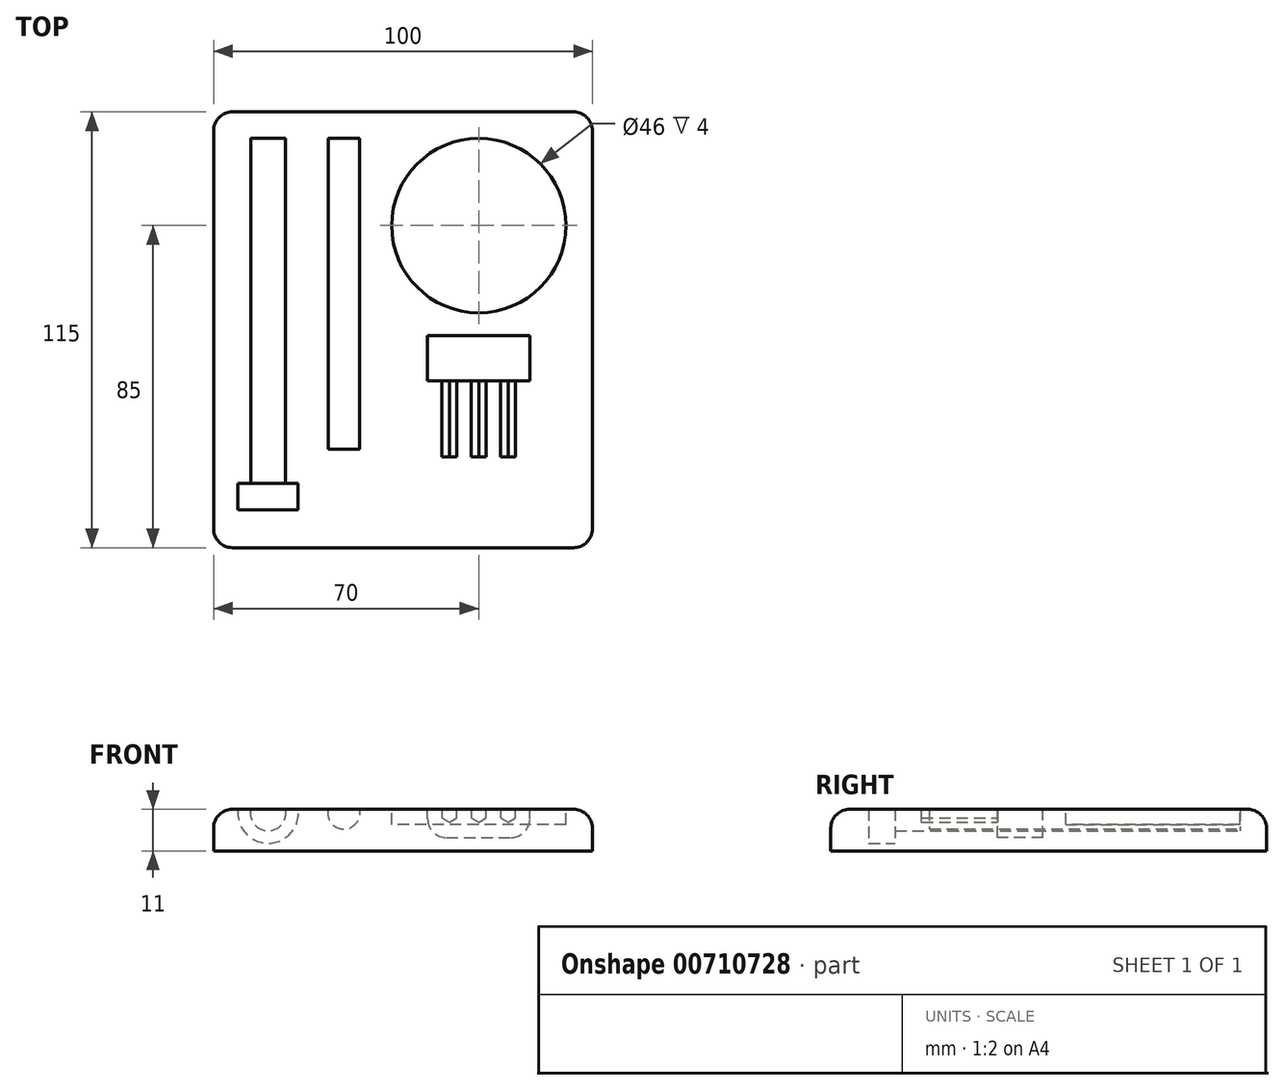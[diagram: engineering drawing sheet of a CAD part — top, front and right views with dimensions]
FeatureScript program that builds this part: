
annotation { "Feature Type Name" : "Feature", "Feature Type Description" : "" }
export const myFeature = defineFeature(function(context is Context, id is Id, definition is map)
    precondition{}
    {
        {
            var Q0;
            Q0=qCreatedBy(makeId("Top.planeOp"),FACE);
            var sketch = newSketch(context, id + "F0", { "sketchPlane" : qUnion([Q0])});
            skLineSegment(sketch, "E0.bottom", {"start": v(0, 0) * mm, "end": v(100, 0) * mm});
            skLineSegment(sketch, "E0.top", {"start": v(0, 115) * mm, "end": v(100, 115) * mm});
            skLineSegment(sketch, "E0.left", {"start": v(0, 0) * mm, "end": v(0, 115) * mm});
            skLineSegment(sketch, "E0.right", {"start": v(100, 0) * mm, "end": v(100, 115) * mm});
            skSolve(sketch);
        }
        {
            var Q0;
            Q0=makeQuery(id+"F0.imprint","IMPRINT",FACE,{"disambiguationData":[TD([[makeQuery(id+"F0.imprint","IMPRINT",EDGE,{"derivedFrom":sQuery(id+"F0.wireOp",EDGE,"E0.bottom")}),1.0]])]});
            extrude(context, id + "F1", {"entities" : qUnion([Q0]), "depth" : 15 * mm, "offsetDistance" : 25 * mm});
        }
        {
            var Q0;
            Q0=makeQuery(id+"F1.opExtrude","CAP_FACE",FACE,{"disambiguationData":[OSD([sQuery(id+"F0.wireOp",EDGE,"E0.bottom"),sQuery(id+"F0.wireOp",EDGE,"E0.top"),sQuery(id+"F0.wireOp",EDGE,"E0.left"),sQuery(id+"F0.wireOp",EDGE,"E0.right")])],"isStart":false});
            var sketch = newSketch(context, id + "F2", { "sketchPlane" : qUnion([Q0])});
            skCircle(sketch, "E1", {"center": v(70, 85) * mm, "radius": 23 * mm});
            skSolve(sketch);
        }
        {
            var Q0;
            Q0=makeQuery(id+"F2.imprint","IMPRINT",FACE,{"disambiguationData":[TD([[makeQuery(id+"F2.imprint","IMPRINT",EDGE,{"derivedFrom":sQuery(id+"F2.wireOp",EDGE,"E1")}),1.0]])]});
            extrude(context, id + "F3", {"entities" : qUnion([Q0]), "operationType" : NewBodyOperationType.REMOVE, "oppositeDirection" : true, "depth" : 4 * mm, "offsetDistance" : 25 * mm});
        }
        {
            var Q0;
            Q0=makeQuery(id+"F1.opExtrude","SWEPT_FACE",FACE,{"disambiguationData":[OSD([sQuery(id+"F0.wireOp",EDGE,"E0.top")])]});
            cPlane(context, id + "F4", {"entities" : qUnion([Q0]), "cplaneType" : CPlaneType.OFFSET, "offset" : 7 * mm, "oppositeDirection" : true, "width" : 150 * mm, "height" : 150 * mm});
        }
        {
            var Q0;
            Q0=qCreatedBy(id+"F4.planeOp",FACE);
            var sketch = newSketch(context, id + "F5", { "sketchPlane" : qUnion([Q0])});
            skCircle(sketch, "E2", {"center": v(-14.4, 14) * mm, "radius": 4.7 * mm});
            skSolve(sketch);
        }
        {
            var Q0;
            Q0=makeQuery(id+"F5.imprint","IMPRINT",FACE,{"disambiguationData":[TD([[makeQuery(id+"F5.imprint","IMPRINT",EDGE,{"derivedFrom":sQuery(id+"F5.wireOp",EDGE,"E2")}),1.0]])]});
            extrude(context, id + "F6", {"entities" : qUnion([Q0]), "operationType" : NewBodyOperationType.REMOVE, "oppositeDirection" : true, "depth" : 91 * mm, "offsetDistance" : 25 * mm});
        }
        {
            var Q0;
            Q0=makeQuery(id+"F6.boolean.opBoolean","COPY",FACE,{"derivedFrom":makeQuery(id+"F6.opExtrude","CAP_FACE",FACE,{"disambiguationData":[OSD([sQuery(id+"F5.wireOp",EDGE,"E2")])],"isStart":false})});
            var sketch = newSketch(context, id + "F7", { "sketchPlane" : qUnion([Q0])});
            skCircle(sketch, "E3", {"center": v(-14.4, 14) * mm, "radius": 8 * mm});
            skSolve(sketch);
        }
        {
            var Q0;
            {var subQ0=sQuery(id+"F5.wireOp",EDGE,"E2");Q0=makeQuery(id+"F7.imprint","IMPRINT",FACE,{"disambiguationData":[TD([[makeQuery(id+"F7.imprint","IMPRINT",EDGE,{"derivedFrom":makeQuery(id+"F6.boolean.opBoolean","COPY",EDGE,{"derivedFrom":makeQuery(id+"F6.opExtrude","CAP_EDGE",EDGE,{"disambiguationData":[OSD([subQ0])],"isStart":false})})}),1.0]])]});}
            var Q1;
            Q1=makeQuery(id+"F7.imprint","IMPRINT",FACE,{"disambiguationData":[TD([[makeQuery(id+"F7.imprint","IMPRINT",EDGE,{"derivedFrom":sQuery(id+"F7.wireOp",EDGE,"E3")}),1.0]])]});
            extrude(context, id + "F8", {"entities" : qUnion([Q0, Q1]), "operationType" : NewBodyOperationType.REMOVE, "oppositeDirection" : true, "depth" : 7 * mm, "offsetDistance" : 25 * mm});
        }
        {
            var Q0;
            Q0=qCreatedBy(id+"F4.planeOp",FACE);
            var sketch = newSketch(context, id + "F9", { "sketchPlane" : qUnion([Q0])});
            skCircle(sketch, "E4", {"center": v(-34.4, 14) * mm, "radius": 4.25 * mm});
            skSolve(sketch);
        }
        {
            var Q0;
            Q0=makeQuery(id+"F9.imprint","IMPRINT",FACE,{"disambiguationData":[TD([[makeQuery(id+"F9.imprint","IMPRINT",EDGE,{"derivedFrom":sQuery(id+"F9.wireOp",EDGE,"E4")}),1.0]])]});
            extrude(context, id + "F10", {"entities" : qUnion([Q0]), "operationType" : NewBodyOperationType.REMOVE, "oppositeDirection" : true, "depth" : 82 * mm, "offsetDistance" : 25 * mm});
        }
        {
            var Q0;
            Q0=makeQuery(id+"F1.opExtrude","CAP_FACE",FACE,{"disambiguationData":[OSD([sQuery(id+"F0.wireOp",EDGE,"E0.bottom"),sQuery(id+"F0.wireOp",EDGE,"E0.top"),sQuery(id+"F0.wireOp",EDGE,"E0.left"),sQuery(id+"F0.wireOp",EDGE,"E0.right")])],"isStart":false});
            var sketch = newSketch(context, id + "F11", { "sketchPlane" : qUnion([Q0])});
            skLineSegment(sketch, "E5.bottom", {"start": v(56.5, 52) * mm, "end": v(83.5, 52) * mm});
            skLineSegment(sketch, "E5.top", {"start": v(56.5, 44) * mm, "end": v(83.5, 44) * mm});
            skLineSegment(sketch, "E5.left", {"start": v(56.5, 52) * mm, "end": v(56.5, 44) * mm});
            skLineSegment(sketch, "E5.right", {"start": v(83.5, 52) * mm, "end": v(83.5, 44) * mm});
            skSolve(sketch);
        }
        {
            var Q0;
            Q0=makeQuery(id+"F11.imprint","IMPRINT",FACE,{"disambiguationData":[TD([[makeQuery(id+"F11.imprint","IMPRINT",EDGE,{"derivedFrom":sQuery(id+"F11.wireOp",EDGE,"E5.bottom")}),-1.0]])]});
            extrude(context, id + "F12", {"entities" : qUnion([Q0]), "operationType" : NewBodyOperationType.REMOVE, "oppositeDirection" : true, "depth" : 7.5 * mm, "offsetDistance" : 25 * mm});
        }
        {
            var Q0;
            Q0=makeQuery(id+"F12.boolean.opBoolean","COPY",FACE,{"derivedFrom":makeQuery(id+"F12.opExtrude","SWEPT_FACE",FACE,{"disambiguationData":[OSD([sQuery(id+"F11.wireOp",EDGE,"E5.top")])]})});
            var sketch = newSketch(context, id + "F13", { "sketchPlane" : qUnion([Q0])});
            skCircle(sketch, "E6.cCircle", {"center": v(-77.78, 13.86) * mm, "radius": 1.98 * mm, "construction": true});
            skLineSegment(sketch, "E6.0", {"start": v(-79.75, 12.72) * mm, "end": v(-79.75, 15) * mm});
            skLineSegment(sketch, "E6.1", {"start": v(-79.75, 15) * mm, "end": v(-77.78, 16.14) * mm});
            skLineSegment(sketch, "E6.2", {"start": v(-77.78, 16.14) * mm, "end": v(-75.8, 15) * mm});
            skLineSegment(sketch, "E6.3", {"start": v(-75.8, 15) * mm, "end": v(-75.8, 12.72) * mm});
            skLineSegment(sketch, "E6.4", {"start": v(-75.8, 12.72) * mm, "end": v(-77.78, 11.58) * mm});
            skLineSegment(sketch, "E6.5", {"start": v(-77.78, 11.58) * mm, "end": v(-79.75, 12.72) * mm});
            skPoint(sketch, "E6.0.midPoint", {"position": v(-79.75, 13.86) * mm});
            skCircle(sketch, "E7.cCircle", {"center": v(-70.03, 13.86) * mm, "radius": 1.98 * mm, "construction": true});
            skPoint(sketch, "E7.cCircle.centerSnap0", {"position": v(-75.8, 13.86) * mm});
            skLineSegment(sketch, "E7.0", {"start": v(-72, 12.72) * mm, "end": v(-72, 15) * mm});
            skLineSegment(sketch, "E7.1", {"start": v(-72, 15) * mm, "end": v(-70.02, 16.14) * mm});
            skLineSegment(sketch, "E7.2", {"start": v(-70.02, 16.14) * mm, "end": v(-68.05, 15) * mm});
            skLineSegment(sketch, "E7.3", {"start": v(-68.05, 15) * mm, "end": v(-68.05, 12.72) * mm});
            skLineSegment(sketch, "E7.4", {"start": v(-68.05, 12.72) * mm, "end": v(-70.03, 11.58) * mm});
            skLineSegment(sketch, "E7.5", {"start": v(-70.03, 11.58) * mm, "end": v(-72, 12.72) * mm});
            skPoint(sketch, "E7.0.midPoint", {"position": v(-72, 13.86) * mm});
            skCircle(sketch, "E8.cCircle", {"center": v(-62.28, 13.86) * mm, "radius": 1.97 * mm, "construction": true});
            skLineSegment(sketch, "E8.0", {"start": v(-64.25, 12.72) * mm, "end": v(-64.25, 15) * mm});
            skLineSegment(sketch, "E8.1", {"start": v(-64.25, 15) * mm, "end": v(-62.28, 16.14) * mm});
            skLineSegment(sketch, "E8.2", {"start": v(-62.28, 16.14) * mm, "end": v(-60.3, 15) * mm});
            skLineSegment(sketch, "E8.3", {"start": v(-60.3, 15) * mm, "end": v(-60.3, 12.72) * mm});
            skLineSegment(sketch, "E8.4", {"start": v(-60.3, 12.72) * mm, "end": v(-62.28, 11.58) * mm});
            skLineSegment(sketch, "E8.5", {"start": v(-62.28, 11.58) * mm, "end": v(-64.25, 12.72) * mm});
            skPoint(sketch, "E8.0.midPoint", {"position": v(-64.25, 13.86) * mm});
            skSolve(sketch);
        }
        {
            var Q0;
            {var subQ5=sQuery(id+"F13.wireOp",EDGE,"E6.0");Q0=makeQuery(id+"F13.imprint","IMPRINT",FACE,{"disambiguationData":[TD([[makeQuery(id+"F13.imprint","IMPRINT",EDGE,{"derivedFrom":subQ5}),-1.0]])]});}
            var Q1;
            {var subQ5=sQuery(id+"F13.wireOp",EDGE,"E7.0");Q1=makeQuery(id+"F13.imprint","IMPRINT",FACE,{"disambiguationData":[TD([[makeQuery(id+"F13.imprint","IMPRINT",EDGE,{"derivedFrom":subQ5}),-1.0]])]});}
            var Q2;
            {var subQ5=sQuery(id+"F13.wireOp",EDGE,"E8.0");Q2=makeQuery(id+"F13.imprint","IMPRINT",FACE,{"disambiguationData":[TD([[makeQuery(id+"F13.imprint","IMPRINT",EDGE,{"derivedFrom":subQ5}),-1.0]])]});}
            extrude(context, id + "F14", {"entities" : qUnion([Q0, Q1, Q2]), "operationType" : NewBodyOperationType.REMOVE, "oppositeDirection" : true, "depth" : 20 * mm, "offsetDistance" : 25 * mm});
        }
        {
            var Q0;
            Q0=makeQuery(id+"F12.boolean.opBoolean","COPY",FACE,{"derivedFrom":makeQuery(id+"F12.opExtrude","SWEPT_FACE",FACE,{"disambiguationData":[OSD([sQuery(id+"F11.wireOp",EDGE,"E5.bottom")])]})});
            extrude(context, id + "F15", {"entities" : qUnion([Q0]), "operationType" : NewBodyOperationType.REMOVE, "oppositeDirection" : true, "depth" : 4 * mm, "offsetDistance" : 25 * mm});
        }
        {
            var Q0;
            Q0=makeQuery(id+"F1.opExtrude","CAP_EDGE",EDGE,{"disambiguationData":[OSD([sQuery(id+"F0.wireOp",EDGE,"E0.bottom")])],"isStart":false});
            var Q1;
            Q1=makeQuery(id+"F1.opExtrude","CAP_EDGE",EDGE,{"disambiguationData":[OSD([sQuery(id+"F0.wireOp",EDGE,"E0.right")])],"isStart":false});
            var Q2;
            Q2=makeQuery(id+"F1.opExtrude","CAP_EDGE",EDGE,{"disambiguationData":[OSD([sQuery(id+"F0.wireOp",EDGE,"E0.top")])],"isStart":false});
            var Q3;
            Q3=makeQuery(id+"F1.opExtrude","CAP_EDGE",EDGE,{"disambiguationData":[OSD([sQuery(id+"F0.wireOp",EDGE,"E0.left")])],"isStart":false});
            var Q4;
            Q4=makeQuery(id+"F1.opExtrude","SWEPT_EDGE",EDGE,{"disambiguationData":[OSD([sQuery(id+"F0.wireOp",EDGE,"E0.top"),sQuery(id+"F0.wireOp",EDGE,"E0.right")])]});
            var Q5;
            Q5=makeQuery(id+"F1.opExtrude","SWEPT_EDGE",EDGE,{"disambiguationData":[OSD([sQuery(id+"F0.wireOp",EDGE,"E0.top"),sQuery(id+"F0.wireOp",EDGE,"E0.left")])]});
            var Q6;
            Q6=makeQuery(id+"F1.opExtrude","SWEPT_EDGE",EDGE,{"disambiguationData":[OSD([sQuery(id+"F0.wireOp",EDGE,"E0.bottom"),sQuery(id+"F0.wireOp",EDGE,"E0.right")])]});
            var Q7;
            Q7=makeQuery(id+"F1.opExtrude","SWEPT_EDGE",EDGE,{"disambiguationData":[OSD([sQuery(id+"F0.wireOp",EDGE,"E0.bottom"),sQuery(id+"F0.wireOp",EDGE,"E0.left")])]});
            var Q8;
            {var subQ0=sQuery(id+"F11.wireOp",EDGE,"E5.left");var subQ1=sQuery(id+"F11.wireOp",EDGE,"E5.bottom");Q8=makeQuery(id+"F15.boolean.opBoolean","MERGE",EDGE,{"derivedFrom":[makeQuery(id+"F12.boolean.opBoolean","COPY",EDGE,{"derivedFrom":makeQuery(id+"F12.opExtrude","CAP_EDGE",EDGE,{"disambiguationData":[OSD([subQ0])],"isStart":false})}),makeQuery(id+"F15.opExtrude","SWEPT_EDGE",EDGE,{"disambiguationData":[OSD([subQ1,subQ0]),TDD([makeQuery(id+"F12.boolean.opBoolean","COPY",VERTEX,{"derivedFrom":makeQuery(id+"F12.opExtrude","CAP_VERTEX",VERTEX,{"disambiguationData":[OSD([subQ1,subQ0])],"isStart":false})})])]})]});}
            var Q9;
            {var subQ0=sQuery(id+"F11.wireOp",EDGE,"E5.right");var subQ1=sQuery(id+"F11.wireOp",EDGE,"E5.bottom");Q9=makeQuery(id+"F15.boolean.opBoolean","MERGE",EDGE,{"derivedFrom":[makeQuery(id+"F12.boolean.opBoolean","COPY",EDGE,{"derivedFrom":makeQuery(id+"F12.opExtrude","CAP_EDGE",EDGE,{"disambiguationData":[OSD([subQ0])],"isStart":false})}),makeQuery(id+"F15.opExtrude","SWEPT_EDGE",EDGE,{"disambiguationData":[OSD([subQ1,subQ0]),TDD([makeQuery(id+"F12.boolean.opBoolean","COPY",VERTEX,{"derivedFrom":makeQuery(id+"F12.opExtrude","CAP_VERTEX",VERTEX,{"disambiguationData":[OSD([subQ1,subQ0])],"isStart":false})})])]})]});}
            fillet(context, id + "F16", {"entities" : qUnion([Q0, Q1, Q2, Q3, Q4, Q5, Q6, Q7, Q8, Q9]), "radius" : 5 * mm, "tangentPropagation" : true, "allowEdgeOverflow" : false});
        }
        {
            var Q0;
            Q0=makeQuery(id+"F1.opExtrude","CAP_FACE",FACE,{"disambiguationData":[OSD([sQuery(id+"F0.wireOp",EDGE,"E0.bottom"),sQuery(id+"F0.wireOp",EDGE,"E0.top"),sQuery(id+"F0.wireOp",EDGE,"E0.left"),sQuery(id+"F0.wireOp",EDGE,"E0.right")])],"isStart":true});
            extrude(context, id + "F17", {"entities" : qUnion([Q0]), "operationType" : NewBodyOperationType.REMOVE, "oppositeDirection" : true, "depth" : 4 * mm, "offsetDistance" : 25 * mm});
        }
    });
